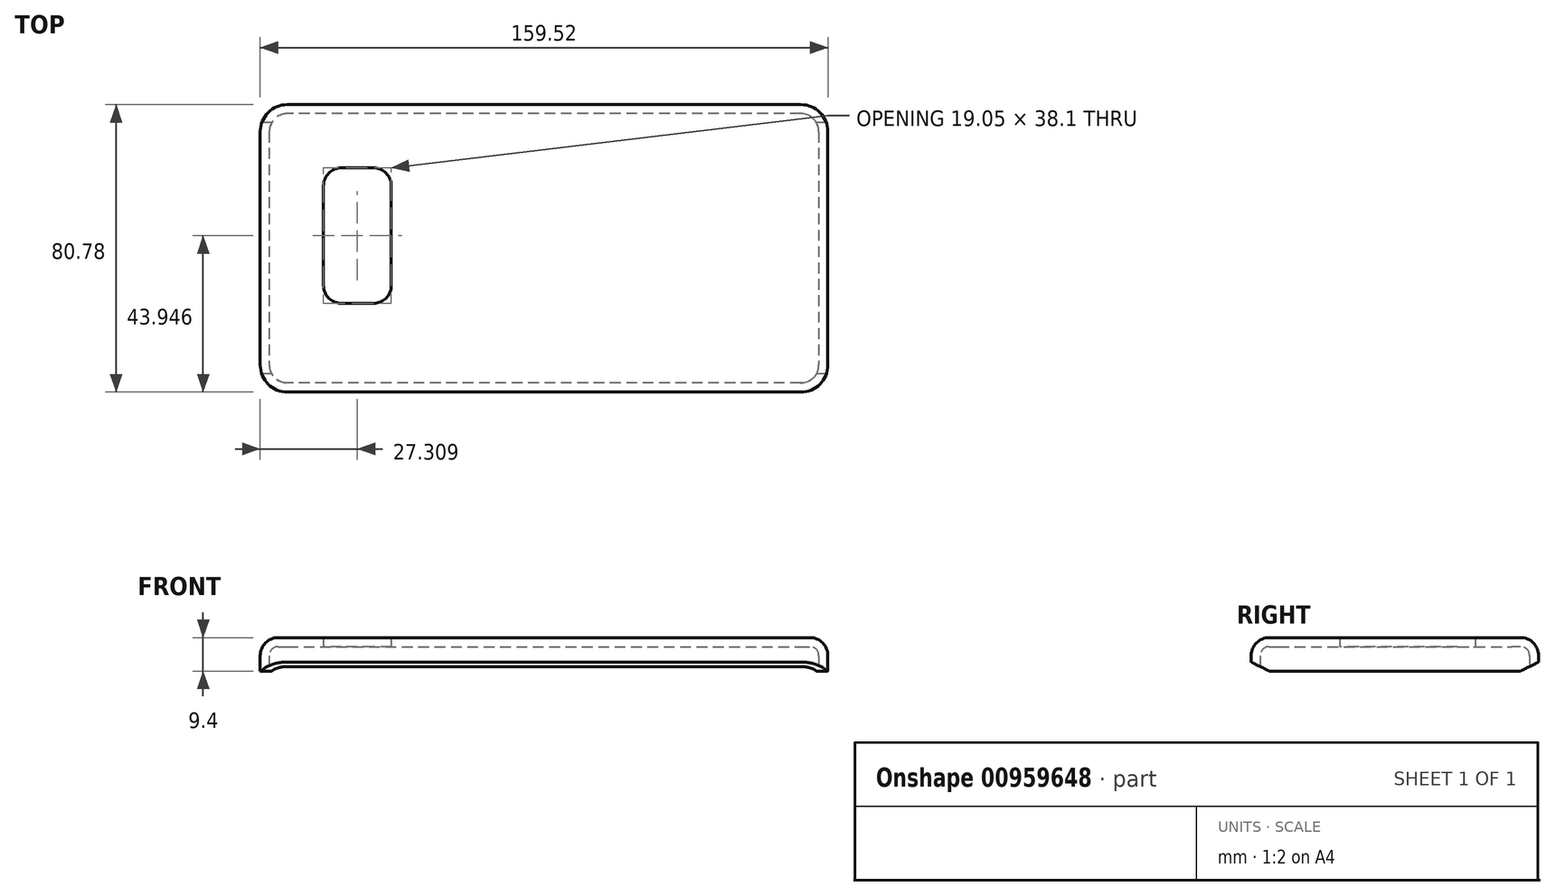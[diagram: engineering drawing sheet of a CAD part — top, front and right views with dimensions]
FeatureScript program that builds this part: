
annotation { "Feature Type Name" : "Feature", "Feature Type Description" : "" }
export const myFeature = defineFeature(function(context is Context, id is Id, definition is map)
    precondition{}
    {
        {
            var Q0;
            Q0=qCreatedBy(makeId("Top.planeOp"),FACE);
            var sketch = newSketch(context, id + "F0", { "sketchPlane" : qUnion([Q0])});
            skLineSegment(sketch, "E0.bottom", {"start": v(79.76, 40.39) * mm, "end": v(-79.76, 40.39) * mm});
            skLineSegment(sketch, "E0.top", {"start": v(79.76, -40.39) * mm, "end": v(-79.76, -40.39) * mm});
            skLineSegment(sketch, "E0.left", {"start": v(79.76, 40.39) * mm, "end": v(79.76, -40.39) * mm});
            skLineSegment(sketch, "E0.right", {"start": v(-79.76, 40.39) * mm, "end": v(-79.76, -40.39) * mm});
            skLineSegment(sketch, "E1", {"start": v(79.76, 40.39) * mm, "end": v(-79.76, -40.39) * mm, "construction": true});
            skSolve(sketch);
        }
        {
            var Q0;
            Q0 = qSketchRegion(id + "F0", true);
            extrude(context, id + "F1", {"entities" : qUnion([Q0]), "depth" : 9.4 * mm, "offsetDistance" : 25.4 * mm});
        }
        {
            var Q0;
            Q0=makeQuery(id+"F1.opExtrude","SWEPT_EDGE",EDGE,{"disambiguationData":[OSD([sQuery(id+"F0.wireOp",EDGE,"E0.top"),sQuery(id+"F0.wireOp",EDGE,"E0.left")])]});
            var Q1;
            Q1=makeQuery(id+"F1.opExtrude","SWEPT_EDGE",EDGE,{"disambiguationData":[OSD([sQuery(id+"F0.wireOp",EDGE,"E0.bottom"),sQuery(id+"F0.wireOp",EDGE,"E0.left")])]});
            var Q2;
            Q2=makeQuery(id+"F1.opExtrude","SWEPT_EDGE",EDGE,{"disambiguationData":[OSD([sQuery(id+"F0.wireOp",EDGE,"E0.top"),sQuery(id+"F0.wireOp",EDGE,"E0.right")])]});
            var Q3;
            Q3=makeQuery(id+"F1.opExtrude","SWEPT_EDGE",EDGE,{"disambiguationData":[OSD([sQuery(id+"F0.wireOp",EDGE,"E0.bottom"),sQuery(id+"F0.wireOp",EDGE,"E0.right")])]});
            fillet(context, id + "F2", {"entities" : qUnion([Q0, Q1, Q2, Q3]), "radius" : 7.62 * mm, "tangentPropagation" : true, "allowEdgeOverflow" : false});
        }
        {
            var Q0;
            Q0=makeQuery(id+"F1.opExtrude","CAP_FACE",FACE,{"disambiguationData":[OSD([sQuery(id+"F0.wireOp",EDGE,"E0.bottom"),sQuery(id+"F0.wireOp",EDGE,"E0.top"),sQuery(id+"F0.wireOp",EDGE,"E0.left"),sQuery(id+"F0.wireOp",EDGE,"E0.right")])],"isStart":false});
            fillet(context, id + "F3", {"entities" : qUnion([Q0]), "radius" : 5.08 * mm, "tangentPropagation" : true, "allowEdgeOverflow" : false});
        }
        {
            var Q0;
            Q0=qCreatedBy(makeId("Right.planeOp"),FACE);
            var sketch = newSketch(context, id + "F4", { "sketchPlane" : qUnion([Q0])});
            skLineSegment(sketch, "E2.bottom", {"start": v(40.39, 0) * mm, "end": v(35.3, 0) * mm});
            skLineSegment(sketch, "E2.left", {"start": v(40.39, 0) * mm, "end": v(40.39, 2.54) * mm});
            skLineSegment(sketch, "E3", {"start": v(35.3, 0) * mm, "end": v(40.39, 2.54) * mm});
            skLineSegment(sketch, "E4", {"start": v(0, 0) * mm, "end": v(0, -26.47) * mm, "construction": true});
            skLineSegment(sketch, "E5.MirrorCS", {"start": v(-35.3, 0) * mm, "end": v(-40.39, 2.54) * mm});
            skLineSegment(sketch, "E6.MirrorCS", {"start": v(-40.39, 0) * mm, "end": v(-35.3, 0) * mm});
            skLineSegment(sketch, "E7.MirrorCS", {"start": v(-40.39, 0) * mm, "end": v(-40.39, 2.54) * mm});
            skSolve(sketch);
        }
        {
            var Q0;
            Q0 = qSketchRegion(id + "F4", true);
            extrude(context, id + "F5", {"entities" : qUnion([Q0]), "operationType" : NewBodyOperationType.REMOVE, "endBound" : BoundingType.THROUGH_ALL, "depth" : 25.4 * mm, "offsetDistance" : 25.4 * mm, "hasSecondDirection" : true, "secondDirectionBound" : SecondDirectionBoundingType.THROUGH_ALL, "secondDirectionOppositeDirection" : true, "secondDirectionDepth" : 25.4 * mm});
        }
        {
            var Q0;
            Q0=makeQuery(id+"F5.boolean.opBoolean","COPY",FACE,{"derivedFrom":makeQuery(id+"F5.opExtrude","SWEPT_FACE",FACE,{"disambiguationData":[OSD([sQuery(id+"F4.wireOp",EDGE,"E5.MirrorCS")])]})});
            var Q1;
            Q1=makeQuery(id+"F5.boolean.opBoolean","COPY",FACE,{"derivedFrom":makeQuery(id+"F5.opExtrude","SWEPT_FACE",FACE,{"disambiguationData":[OSD([sQuery(id+"F4.wireOp",EDGE,"E3")])]})});
            var Q2;
            Q2=makeQuery(id+"F1.opExtrude","CAP_FACE",FACE,{"disambiguationData":[OSD([sQuery(id+"F0.wireOp",EDGE,"E0.bottom"),sQuery(id+"F0.wireOp",EDGE,"E0.top"),sQuery(id+"F0.wireOp",EDGE,"E0.left"),sQuery(id+"F0.wireOp",EDGE,"E0.right")])],"isStart":true});
            shell(context, id + "F6", {"entities" : qUnion([Q0, Q1, Q2]), "thickness" : 2.54 * mm});
        }
        {
            var Q0;
            Q0=qCreatedBy(makeId("Top.planeOp"),FACE);
            var sketch = newSketch(context, id + "F7", { "sketchPlane" : qUnion([Q0])});
            skLineSegment(sketch, "E8.bottom", {"start": v(-61.98, -15.5) * mm, "end": v(-42.93, -15.5) * mm});
            skLineSegment(sketch, "E8.top", {"start": v(-61.98, 22.6) * mm, "end": v(-42.93, 22.6) * mm});
            skLineSegment(sketch, "E8.left", {"start": v(-61.98, -15.5) * mm, "end": v(-61.98, 22.6) * mm});
            skLineSegment(sketch, "E8.right", {"start": v(-42.93, -15.5) * mm, "end": v(-42.93, 22.6) * mm});
            skSolve(sketch);
        }
        {
            var Q0;
            Q0=makeQuery(id+"F7.imprint","IMPRINT",FACE,{"disambiguationData":[TD([[makeQuery(id+"F7.imprint","IMPRINT",EDGE,{"derivedFrom":sQuery(id+"F7.wireOp",EDGE,"E8.bottom")}),1.0]])]});
            extrude(context, id + "F8", {"entities" : qUnion([Q0]), "operationType" : NewBodyOperationType.REMOVE, "depth" : 30.48 * mm, "offsetDistance" : 25.4 * mm});
        }
        {
            var Q0;
            Q0=makeQuery(id+"F8.boolean.opBoolean","COPY",EDGE,{"derivedFrom":makeQuery(id+"F8.opExtrude","SWEPT_EDGE",EDGE,{"disambiguationData":[OSD([sQuery(id+"F7.wireOp",EDGE,"E8.bottom"),sQuery(id+"F7.wireOp",EDGE,"E8.left")])]})});
            var Q1;
            Q1=makeQuery(id+"F8.boolean.opBoolean","COPY",EDGE,{"derivedFrom":makeQuery(id+"F8.opExtrude","SWEPT_EDGE",EDGE,{"disambiguationData":[OSD([sQuery(id+"F7.wireOp",EDGE,"E8.bottom"),sQuery(id+"F7.wireOp",EDGE,"E8.right")])]})});
            var Q2;
            Q2=makeQuery(id+"F8.boolean.opBoolean","COPY",EDGE,{"derivedFrom":makeQuery(id+"F8.opExtrude","SWEPT_EDGE",EDGE,{"disambiguationData":[OSD([sQuery(id+"F7.wireOp",EDGE,"E8.top"),sQuery(id+"F7.wireOp",EDGE,"E8.left")])]})});
            var Q3;
            Q3=makeQuery(id+"F8.boolean.opBoolean","COPY",EDGE,{"derivedFrom":makeQuery(id+"F8.opExtrude","SWEPT_EDGE",EDGE,{"disambiguationData":[OSD([sQuery(id+"F7.wireOp",EDGE,"E8.top"),sQuery(id+"F7.wireOp",EDGE,"E8.right")])]})});
            fillet(context, id + "F9", {"entities" : qUnion([Q0, Q1, Q2, Q3]), "radius" : 5.08 * mm, "tangentPropagation" : true, "allowEdgeOverflow" : false});
        }
    });
